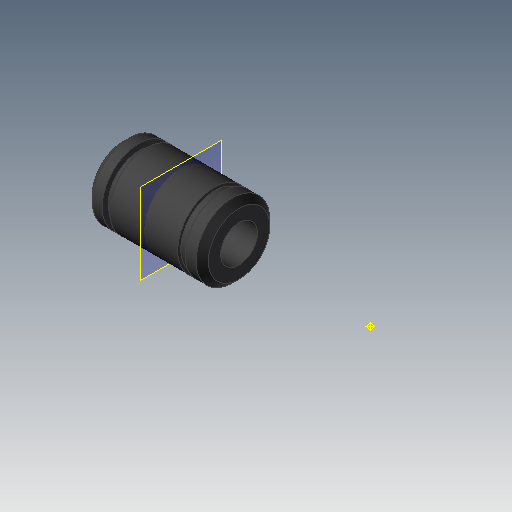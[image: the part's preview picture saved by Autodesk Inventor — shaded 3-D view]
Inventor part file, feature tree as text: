
AUTODESK INVENTOR PART (.ipt)
format: ipt  version: 2019.4 (Build 234330000, 330)  size: 136,192 bytes
history: native  units: in
note: dims shown in document units (in); Inventor stores cm internally (conversion verified against a paired STEP export)
features: other x3, plane x3, revolve x1, chamfer x1, sketch x1
ambient origin geometry x8: Origin, YZ Plane, XZ Plane, XY Plane, X Axis, Y Axis, Z Axis, Center Point
bodies: Solid1 (feature_tree)
feature tree (9):
  revolve  "Revolution1"  [1 undecoded]
  chamfer  "Chamfer1"  Distance=0.2362in
  other  "Work Point1"
  sketch  "Sketch1"  dims[d0=0.7441in d1=0.0in d2=0.2362in d3=0.1024in d4=0.0394in d5=0.0472in d6=0.1102in d7=0.0472in d8=0.1181in d9=90.0deg d10=0.0394in d11=0.125in d12=45.0deg]
  plane  "Work Plane1"
  plane  "Work Plane2"
  plane  "Work Plane3"
  other  "Opentrons_Microscope_v0.iam"
  other  "00_MTP_96-welplate:1"
note: 1 required parameter value undecoded (feature->parameter linkage not recoverable at this tier; creation-order binding heuristic only, values carry confidence <= 0.55)
